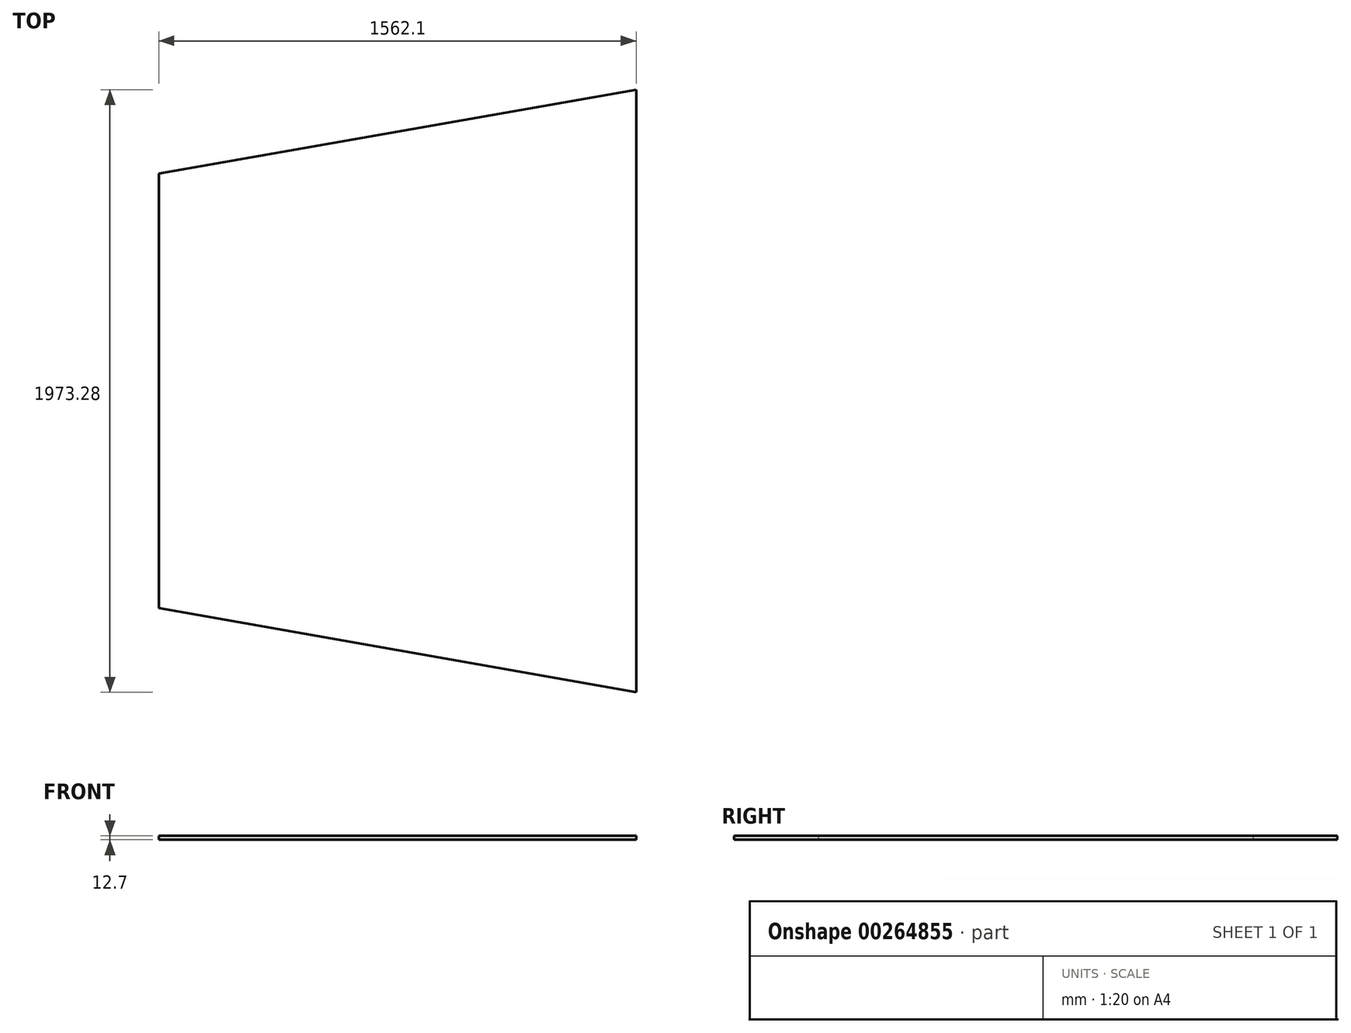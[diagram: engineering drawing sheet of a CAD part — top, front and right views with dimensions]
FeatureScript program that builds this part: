
annotation { "Feature Type Name" : "Feature", "Feature Type Description" : "" }
export const myFeature = defineFeature(function(context is Context, id is Id, definition is map)
    precondition{}
    {
        {
            var Q0;
            Q0=qCreatedBy(makeId("Top.planeOp"),FACE);
            var sketch = newSketch(context, id + "F0", { "sketchPlane" : qUnion([Q0])});
            skLineSegment(sketch, "E0.left", {"start": v(-807.9, 745.02) * mm, "end": v(-807.9, 33.82) * mm});
            skLineSegment(sketch, "E1.10.0.1", {"start": v(754.2, 1020.46) * mm, "end": v(754.2, 33.82) * mm});
            skLineSegment(sketch, "E2", {"start": v(-807.9, 745.02) * mm, "end": v(754.2, 1020.46) * mm});
            skLineSegment(sketch, "E3", {"start": v(-807.9, 33.82) * mm, "end": v(754.2, 33.82) * mm});
            skSolve(sketch);
        }
        {
            var Q0;
            Q0=makeQuery(id+"F0.imprint","IMPRINT",FACE,{"disambiguationData":[TD([[makeQuery(id+"F0.imprint","IMPRINT",EDGE,{"derivedFrom":sQuery(id+"F0.wireOp",EDGE,"E0.left")}),1.0]])]});
            extrude(context, id + "F1", {"entities" : qUnion([Q0]), "depth" : 12.7 * mm, "offsetDistance" : 25.4 * mm});
        }
        {
            var Q0;
            Q0=makeQuery(id+"F1.opExtrude","SWEPT_BODY",BODY,{"disambiguationData":[OSD([sQuery(id+"F0.wireOp",EDGE,"E0.left"),sQuery(id+"F0.wireOp",EDGE,"E1.10.0.1"),sQuery(id+"F0.wireOp",EDGE,"E2"),sQuery(id+"F0.wireOp",EDGE,"E3")])]});
            var Q1;
            Q1=makeQuery(id+"F1.opExtrude","SWEPT_FACE",FACE,{"disambiguationData":[OSD([sQuery(id+"F0.wireOp",EDGE,"E3")])]});
            mirror(context, id + "F2", {"operationType" : NewBodyOperationType.ADD, "entities" : qUnion([Q0]), "mirrorPlane" : qUnion([Q1])});
        }
    });
